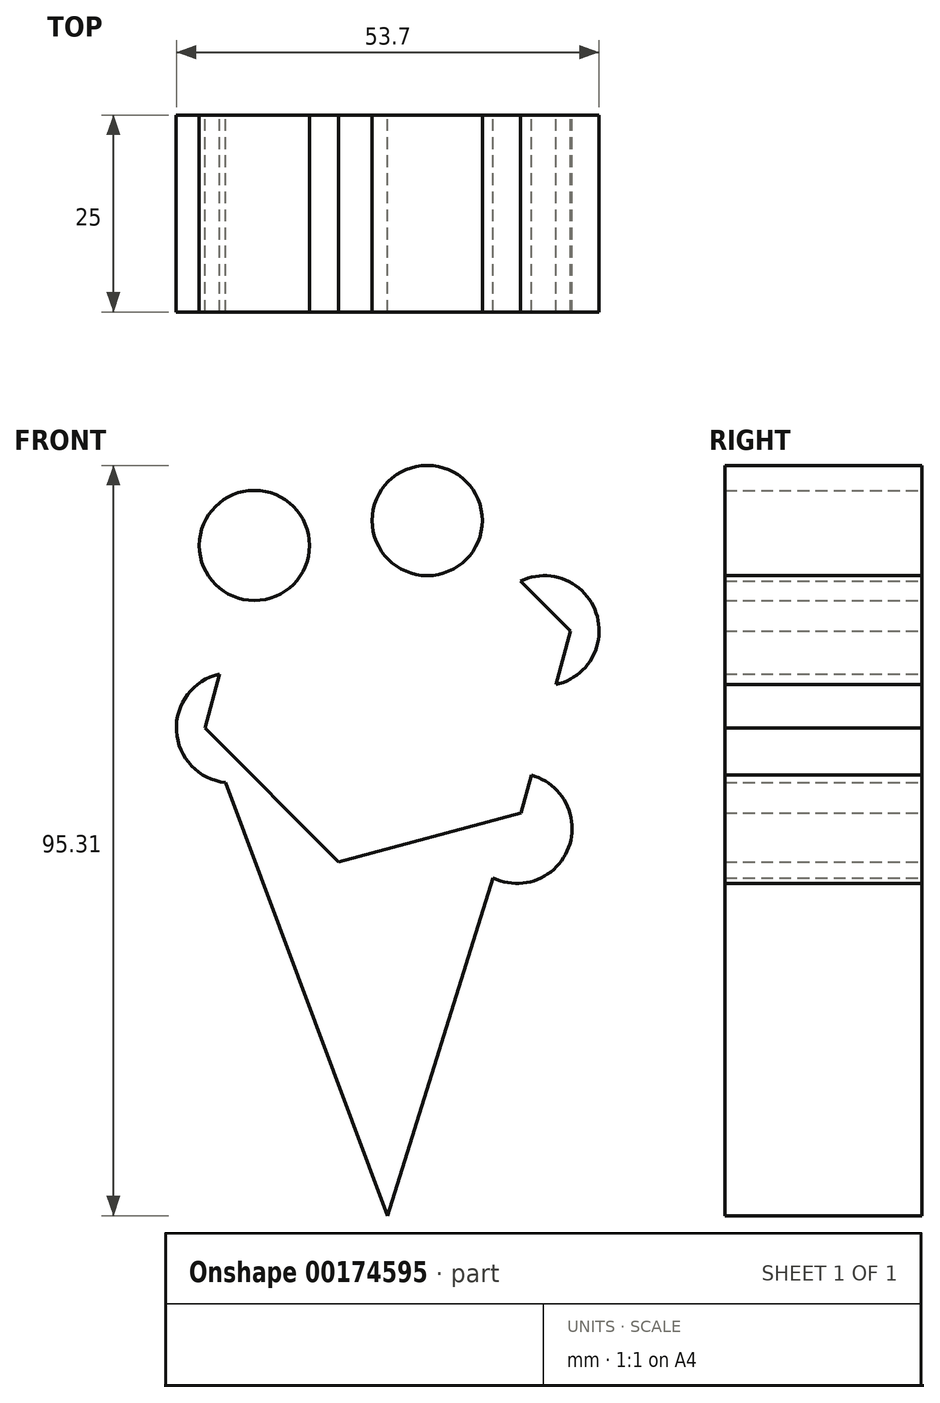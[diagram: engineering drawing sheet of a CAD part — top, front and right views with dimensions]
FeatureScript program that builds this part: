
annotation { "Feature Type Name" : "Feature", "Feature Type Description" : "" }
export const myFeature = defineFeature(function(context is Context, id is Id, definition is map)
    precondition{}
    {
        {
            var Q0;
            Q0=qCreatedBy(makeId("Front.planeOp"),FACE);
            var sketch = newSketch(context, id + "F0", { "sketchPlane" : qUnion([Q0])});
            skCircle(sketch, "E0.cCircle", {"center": v(0, 35.56) * mm, "radius": 20.79 * mm, "construction": true});
            skLineSegment(sketch, "E0.0", {"start": v(16.94, 18.55) * mm, "end": v(-6.26, 12.38) * mm});
            skLineSegment(sketch, "E0.1", {"start": v(-6.26, 12.38) * mm, "end": v(-23.2, 29.4) * mm});
            skLineSegment(sketch, "E0.2", {"start": v(-23.2, 29.4) * mm, "end": v(-16.94, 52.57) * mm});
            skLineSegment(sketch, "E0.3", {"start": v(-16.94, 52.57) * mm, "end": v(6.26, 58.73) * mm});
            skLineSegment(sketch, "E0.4", {"start": v(6.26, 58.73) * mm, "end": v(23.2, 41.72) * mm});
            skLineSegment(sketch, "E0.5", {"start": v(23.2, 41.72) * mm, "end": v(16.94, 18.55) * mm});
            skPoint(sketch, "E0.0.midPoint", {"position": v(5.34, 15.47) * mm});
            skArc(sketch, "E1", {"start": v(5.02, 55.73) * mm, "mid": v(5.01, 57.04) * mm, "end": v(4.66, 58.3) * mm});
            skCircle(sketch, "E2", {"center": v(19.85, 41.72) * mm, "radius": 7 * mm});
            skCircle(sketch, "E3", {"center": v(16.42, 16.62) * mm, "radius": 7 * mm});
            skCircle(sketch, "E4", {"center": v(-6.26, 15.73) * mm, "radius": 7 * mm});
            skCircle(sketch, "E5", {"center": v(-19.85, 29.4) * mm, "radius": 7 * mm});
            skCircle(sketch, "E6", {"center": v(-16.94, 52.57) * mm, "radius": 7 * mm});
            skArc(sketch, "E7.trimOffspring", {"start": v(-5.02, 55.73) * mm, "mid": v(-5.02, 55.73) * mm, "end": v(-5.02, 55.73) * mm});
            skCircle(sketch, "E8", {"center": v(5.02, 55.73) * mm, "radius": 7 * mm});
            skLineSegment(sketch, "E9", {"start": v(-23.2, 29.4) * mm, "end": v(0, -32.58) * mm});
            skLineSegment(sketch, "E10", {"start": v(23.2, 41.72) * mm, "end": v(0, -32.58) * mm});
            skSolve(sketch);
        }
        {
            var Q0;
            {var subQ0=sQuery(id+"F0.wireOp",EDGE,"E0.3");var subQ1=sQuery(id+"F0.wireOp",EDGE,"E0.2");var subQ2=makeQuery(id+"F0.imprint","INTERSECT",VERTEX,{"derivedFrom":[subQ1,subQ0]});Q0=makeQuery(id+"F0.imprint","IMPRINT",FACE,{"disambiguationData":[TD([[makeQuery(id+"F0.imprint","IMPRINT",EDGE,{"disambiguationData":[TD([[subQ2,1.0]])],"derivedFrom":subQ1}),1.0]])]});}
            var Q1;
            {var subQ1=sQuery(id+"F0.wireOp",EDGE,"E0.4");var subQ3=sQuery(id+"F0.wireOp",EDGE,"E2");var subQ4=makeQuery(id+"F0.imprint","INTERSECT",VERTEX,{"derivedFrom":[subQ1,subQ3]});Q1=makeQuery(id+"F0.imprint","IMPRINT",FACE,{"disambiguationData":[TD([[makeQuery(id+"F0.imprint","IMPRINT",EDGE,{"disambiguationData":[TD([[subQ4,1.0]])],"derivedFrom":subQ3}),1.0]])]});}
            var Q2;
            {var subQ0=sQuery(id+"F0.wireOp",EDGE,"E0.3");var subQ1=makeQuery(id+"F0.imprint","IMPRINT",VERTEX,{"disambiguationData":[OD(0.0)],"derivedFrom":subQ0});Q2=makeQuery(id+"F0.imprint","IMPRINT",FACE,{"disambiguationData":[TD([[makeQuery(id+"F0.imprint","IMPRINT",EDGE,{"disambiguationData":[TD([[subQ1,1.0]])],"derivedFrom":subQ0}),1.0]])]});}
            var Q3;
            {var subQ0=sQuery(id+"F0.wireOp",EDGE,"E0.5");var subQ1=sQuery(id+"F0.wireOp",EDGE,"E0.0");var subQ2=makeQuery(id+"F0.imprint","INTERSECT",VERTEX,{"derivedFrom":[subQ1,subQ0]});Q3=makeQuery(id+"F0.imprint","IMPRINT",FACE,{"disambiguationData":[TD([[makeQuery(id+"F0.imprint","IMPRINT",EDGE,{"disambiguationData":[TD([[subQ2,-1.0]])],"derivedFrom":subQ1}),1.0]])]});}
            var Q4;
            {var subQ0=sQuery(id+"F0.wireOp",EDGE,"E0.1");var subQ1=sQuery(id+"F0.wireOp",EDGE,"E0.0");var subQ2=makeQuery(id+"F0.imprint","INTERSECT",VERTEX,{"derivedFrom":[subQ1,subQ0]});Q4=makeQuery(id+"F0.imprint","IMPRINT",FACE,{"disambiguationData":[TD([[makeQuery(id+"F0.imprint","IMPRINT",EDGE,{"disambiguationData":[TD([[subQ2,1.0]])],"derivedFrom":subQ1}),1.0]])]});}
            var Q5;
            {var subQ1=sQuery(id+"F0.wireOp",EDGE,"E0.2");var subQ3=sQuery(id+"F0.wireOp",EDGE,"E5");var subQ4=makeQuery(id+"F0.imprint","INTERSECT",VERTEX,{"derivedFrom":[subQ1,subQ3]});Q5=makeQuery(id+"F0.imprint","IMPRINT",FACE,{"disambiguationData":[TD([[makeQuery(id+"F0.imprint","IMPRINT",EDGE,{"disambiguationData":[TD([[subQ4,-1.0]])],"derivedFrom":subQ3}),1.0]])]});}
            var Q6;
            {var subQ0=sQuery(id+"F0.wireOp",EDGE,"E9");var subQ3=sQuery(id+"F0.wireOp",EDGE,"E5");var subQ5=makeQuery(id+"F0.imprint","INTERSECT",VERTEX,{"derivedFrom":[subQ3,subQ0]});Q6=makeQuery(id+"F0.imprint","IMPRINT",FACE,{"disambiguationData":[TD([[makeQuery(id+"F0.imprint","IMPRINT",EDGE,{"disambiguationData":[TD([[subQ5,-1.0]])],"derivedFrom":subQ3}),1.0]])]});}
            var Q7;
            {var subQ0=sQuery(id+"F0.wireOp",EDGE,"E10");var subQ1=sQuery(id+"F0.wireOp",EDGE,"E0.0");var subQ2=makeQuery(id+"F0.imprint","INTERSECT",VERTEX,{"derivedFrom":[subQ1,subQ0]});Q7=makeQuery(id+"F0.imprint","IMPRINT",FACE,{"disambiguationData":[TD([[makeQuery(id+"F0.imprint","IMPRINT",EDGE,{"disambiguationData":[TD([[subQ2,-1.0]])],"derivedFrom":subQ1}),1.0]])]});}
            var Q8;
            {var subQ0=sQuery(id+"F0.wireOp",EDGE,"E0.3");var subQ1=makeQuery(id+"F0.imprint","IMPRINT",VERTEX,{"disambiguationData":[OD(0.0)],"derivedFrom":subQ0});Q8=makeQuery(id+"F0.imprint","IMPRINT",FACE,{"disambiguationData":[TD([[makeQuery(id+"F0.imprint","IMPRINT",EDGE,{"disambiguationData":[TD([[subQ1,1.0]])],"derivedFrom":subQ0}),-1.0]])]});}
            var Q9;
            {var subQ0=sQuery(id+"F0.wireOp",EDGE,"E0.3");var subQ1=sQuery(id+"F0.wireOp",EDGE,"E0.2");var subQ2=makeQuery(id+"F0.imprint","INTERSECT",VERTEX,{"derivedFrom":[subQ1,subQ0]});Q9=makeQuery(id+"F0.imprint","IMPRINT",FACE,{"disambiguationData":[TD([[makeQuery(id+"F0.imprint","IMPRINT",EDGE,{"disambiguationData":[TD([[subQ2,1.0]])],"derivedFrom":subQ1}),-1.0]])]});}
            var Q10;
            {var subQ1=sQuery(id+"F0.wireOp",EDGE,"E0.0");var subQ6=sQuery(id+"F0.wireOp",EDGE,"E3");var subQ8=makeQuery(id+"F0.imprint","INTERSECT",VERTEX,{"derivedFrom":[subQ1,subQ6]});Q10=makeQuery(id+"F0.imprint","IMPRINT",FACE,{"disambiguationData":[TD([[makeQuery(id+"F0.imprint","IMPRINT",EDGE,{"disambiguationData":[TD([[subQ8,-1.0]])],"derivedFrom":subQ1}),1.0]])]});}
            extrude(context, id + "F1", {"entities" : qUnion([Q0, Q1, Q2, Q3, Q4, Q5, Q6, Q7, Q8, Q9, Q10]), "depth" : 25 * mm});
        }
    });
